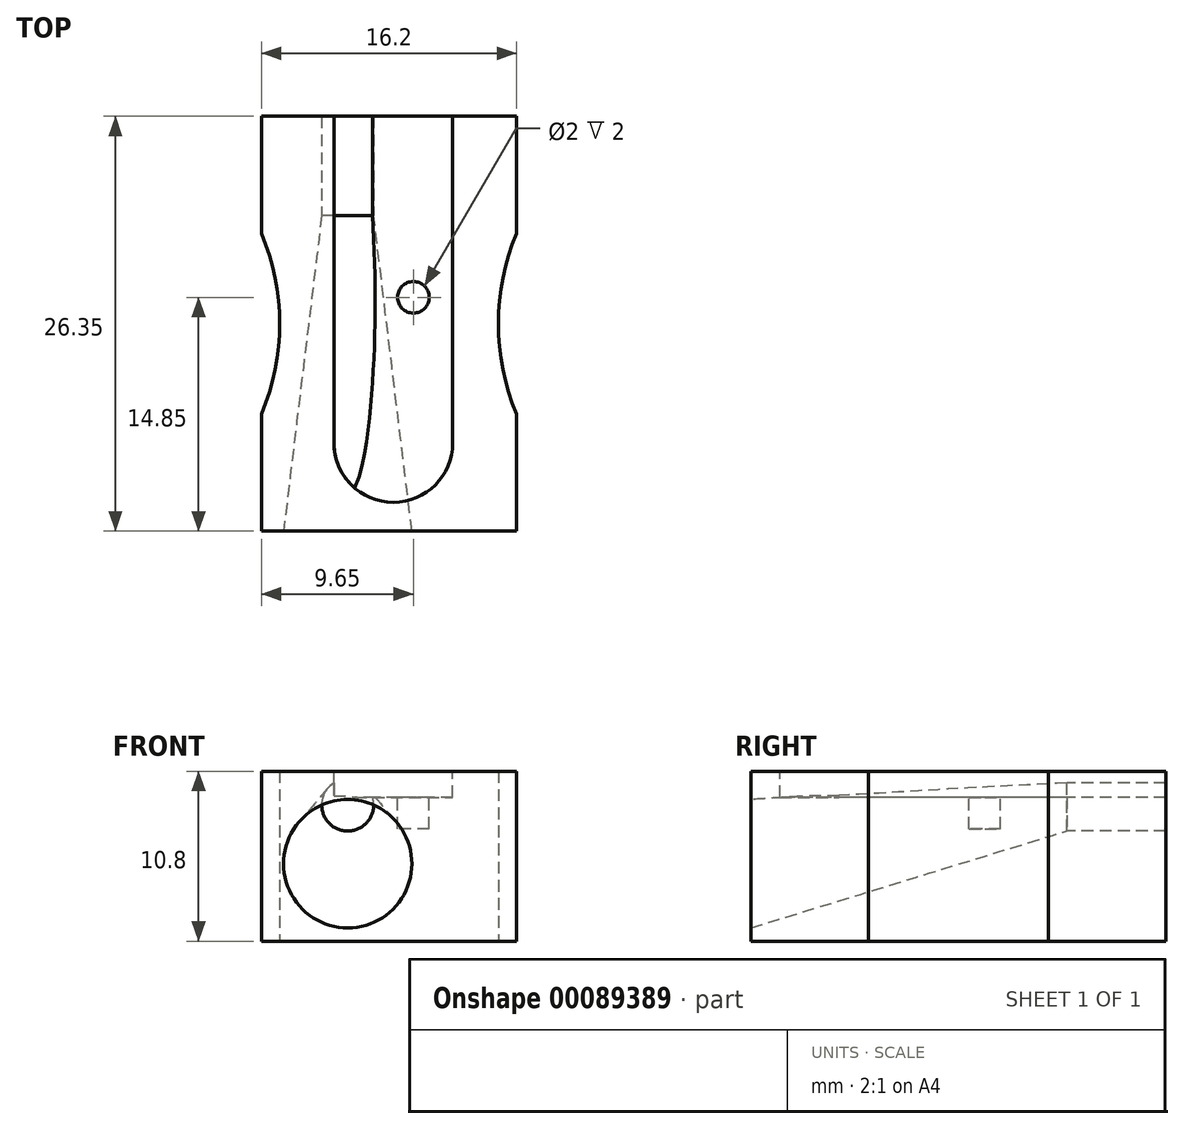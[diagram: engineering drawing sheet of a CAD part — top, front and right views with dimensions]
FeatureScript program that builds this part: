
annotation { "Feature Type Name" : "Feature", "Feature Type Description" : "" }
export const myFeature = defineFeature(function(context is Context, id is Id, definition is map)
    precondition{}
    {
        {
            var Q0;
            Q0=qCreatedBy(makeId("Top.planeOp"),FACE);
            var sketch = newSketch(context, id + "F0", { "sketchPlane" : qUnion([Q0])});
            skLineSegment(sketch, "E0", {"start": v(0, 0) * mm, "end": v(0, 26.35) * mm});
            skLineSegment(sketch, "E1", {"start": v(0, 26.35) * mm, "end": v(-8.1, 26.35) * mm});
            skLineSegment(sketch, "E2", {"start": v(-8.1, 26.35) * mm, "end": v(-8.1, 18.9) * mm});
            skLineSegment(sketch, "E3", {"start": v(-8.1, 0) * mm, "end": v(0, 0) * mm});
            skLineSegment(sketch, "E4", {"start": v(0, 13.18) * mm, "end": v(-21.65, 13.17) * mm, "construction": true});
            skArc(sketch, "E5", {"start": v(-8.1, 7.45) * mm, "mid": v(-6.94, 13.17) * mm, "end": v(-8.1, 18.9) * mm});
            skLineSegment(sketch, "E6.trimOffspring", {"start": v(-8.1, 7.45) * mm, "end": v(-8.1, 0) * mm});
            skPoint(sketch, "E7", {"position": v(-6.94, 13.17) * mm});
            skSolve(sketch);
        }
        {
            var Q0;
            Q0 = qSketchRegion(id + "F0", true);
            extrude(context, id + "F1", {"entities" : qUnion([Q0]), "depth" : 10.8 * mm});
        }
        {
            var Q0;
            Q0=makeQuery(id+"F1.opExtrude","SWEPT_BODY",BODY,{"disambiguationData":[OSD([sQuery(id+"F0.wireOp",EDGE,"E0"),sQuery(id+"F0.wireOp",EDGE,"E1"),sQuery(id+"F0.wireOp",EDGE,"E2"),sQuery(id+"F0.wireOp",EDGE,"E3"),sQuery(id+"F0.wireOp",EDGE,"E5"),sQuery(id+"F0.wireOp",EDGE,"E6.trimOffspring")])]});
            var Q1;
            Q1=qCreatedBy(makeId("Right.planeOp"),FACE);
            mirror(context, id + "F2", {"operationType" : NewBodyOperationType.ADD, "entities" : qUnion([Q0]), "mirrorPlane" : qUnion([Q1])});
        }
        {
            var Q0;
            {var subQ0=makeQuery(id+"F1.opExtrude","CAP_FACE",FACE,{"disambiguationData":[OSD([sQuery(id+"F0.wireOp",EDGE,"E0"),sQuery(id+"F0.wireOp",EDGE,"E1"),sQuery(id+"F0.wireOp",EDGE,"E2"),sQuery(id+"F0.wireOp",EDGE,"E3"),sQuery(id+"F0.wireOp",EDGE,"E5"),sQuery(id+"F0.wireOp",EDGE,"E6.trimOffspring")])],"isStart":false});Q0=makeQuery(id+"F2.boolean.opBoolean","MERGE",FACE,{"derivedFrom":[subQ0,makeQuery(id+"F2.opPattern","COPY",FACE,{"derivedFrom":subQ0,"instanceName":"1"})]});}
            var sketch = newSketch(context, id + "F3", { "sketchPlane" : qUnion([Q0])});
            skLineSegment(sketch, "E8", {"start": v(-3.5, 26.35) * mm, "end": v(-3.5, 5.6) * mm});
            skLineSegment(sketch, "E9", {"start": v(4.05, 26.35) * mm, "end": v(4.05, 5.6) * mm});
            skArc(sketch, "E10", {"start": v(-3.5, 5.6) * mm, "mid": v(0.28, 1.83) * mm, "end": v(4.05, 5.6) * mm});
            skLineSegment(sketch, "E11", {"start": v(-3.5, 26.35) * mm, "end": v(4.05, 26.35) * mm});
            skSolve(sketch);
        }
        {
            var Q0;
            {var subQ0=makeQuery(id+"F1.opExtrude","SWEPT_FACE",FACE,{"disambiguationData":[OSD([sQuery(id+"F0.wireOp",EDGE,"E3")])]});Q0=makeQuery(id+"F2.boolean.opBoolean","MERGE",FACE,{"derivedFrom":[subQ0,makeQuery(id+"F2.opPattern","COPY",FACE,{"derivedFrom":subQ0,"instanceName":"1"})]});}
            var sketch = newSketch(context, id + "F4", { "sketchPlane" : qUnion([Q0])});
            skCircle(sketch, "E12", {"center": v(-2.63, 4.92) * mm, "radius": 4.08 * mm});
            skSolve(sketch);
        }
        {
            var Q0;
            {var subQ0=makeQuery(id+"F1.opExtrude","SWEPT_FACE",FACE,{"disambiguationData":[OSD([sQuery(id+"F0.wireOp",EDGE,"E1")])]});Q0=makeQuery(id+"F2.boolean.opBoolean","MERGE",FACE,{"derivedFrom":[subQ0,makeQuery(id+"F2.opPattern","COPY",FACE,{"derivedFrom":subQ0,"instanceName":"1"})]});}
            var sketch = newSketch(context, id + "F5", { "sketchPlane" : qUnion([Q0])});
            skCircle(sketch, "E13", {"center": v(2.63, 8.65) * mm, "radius": 1.65 * mm});
            skSolve(sketch);
        }
        {
            var Q0;
            {var subQ0=makeQuery(id+"F1.opExtrude","SWEPT_FACE",FACE,{"disambiguationData":[OSD([sQuery(id+"F0.wireOp",EDGE,"E1")])]});Q0=makeQuery(id+"F2.boolean.opBoolean","MERGE",FACE,{"derivedFrom":[subQ0,makeQuery(id+"F2.opPattern","COPY",FACE,{"derivedFrom":subQ0,"instanceName":"1"})]});}
            cPlane(context, id + "F6", {"entities" : qUnion([Q0]), "cplaneType" : CPlaneType.OFFSET, "offset" : 6.3 * mm, "oppositeDirection" : true, "width" : 150 * mm, "height" : 150 * mm});
        }
        {
            var Q0;
            Q0=qCreatedBy(id+"F6.planeOp",FACE);
            var sketch = newSketch(context, id + "F7", { "sketchPlane" : qUnion([Q0])});
            skCircle(sketch, "E14", {"center": v(2.63, 8.65) * mm, "radius": 1.65 * mm});
            skSolve(sketch);
        }
        {
            var Q1;
            Q1 = qSketchRegion(id + "F4", true);
            var Q2;
            Q2 = qSketchRegion(id + "F7", true);
            loft(context, id + "F8", {"operationType" : NewBodyOperationType.REMOVE, "sheetProfilesArray" : [{ "sheetProfileEntities" : qUnion([Q1]) }, { "sheetProfileEntities" : qUnion([Q2]) }]});
        }
        {
            var Q0;
            Q0=makeQuery(id+"F3.imprint","IMPRINT",FACE,{"disambiguationData":[TD([[makeQuery(id+"F3.imprint","IMPRINT",EDGE,{"derivedFrom":sQuery(id+"F3.wireOp",EDGE,"E8")}),1.0]])]});
            extrude(context, id + "F9", {"entities" : qUnion([Q0]), "operationType" : NewBodyOperationType.REMOVE, "oppositeDirection" : true, "depth" : 1.65 * mm});
        }
        {
            var Q0;
            Q0=sQuery(id+"F7.wireOp",VERTEX,"E14.center");
            var Q1;
            Q1=sQuery(id+"F5.wireOp",VERTEX,"E13.center");
            var Q2;
            Q2=makeQuery(id+"F1.opExtrude","SWEPT_BODY",BODY,{"disambiguationData":[OSD([sQuery(id+"F0.wireOp",EDGE,"E0"),sQuery(id+"F0.wireOp",EDGE,"E1"),sQuery(id+"F0.wireOp",EDGE,"E2"),sQuery(id+"F0.wireOp",EDGE,"E3"),sQuery(id+"F0.wireOp",EDGE,"E5"),sQuery(id+"F0.wireOp",EDGE,"E6.trimOffspring")])]});
            hole(context, id + "F10", {"style" : HoleStyle.SIMPLE, "endStyle" : HoleEndStyle.THROUGH, "oppositeDirection" : true, "holeDiameter" : 3.3 * mm, "locations" : qUnion([Q0, Q1]), "scope" : qUnion([Q2]), "isTappedThrough" : true});
        }
        {
            var Q0;
            Q0=makeQuery(id+"F9.boolean.opBoolean","COPY",FACE,{"derivedFrom":makeQuery(id+"F9.opExtrude","CAP_FACE",FACE,{"disambiguationData":[OSD([sQuery(id+"F3.wireOp",EDGE,"E8"),sQuery(id+"F3.wireOp",EDGE,"E9"),sQuery(id+"F3.wireOp",EDGE,"E10"),sQuery(id+"F3.wireOp",EDGE,"E11")])],"isStart":false})});
            var sketch = newSketch(context, id + "F11", { "sketchPlane" : qUnion([Q0])});
            skCircle(sketch, "E15", {"center": v(1.55, 14.85) * mm, "radius": 1 * mm});
            skSolve(sketch);
        }
        {
            var Q0;
            Q0 = qSketchRegion(id + "F11", true);
            extrude(context, id + "F12", {"entities" : qUnion([Q0]), "operationType" : NewBodyOperationType.REMOVE, "oppositeDirection" : true, "depth" : 2 * mm});
        }
    });
